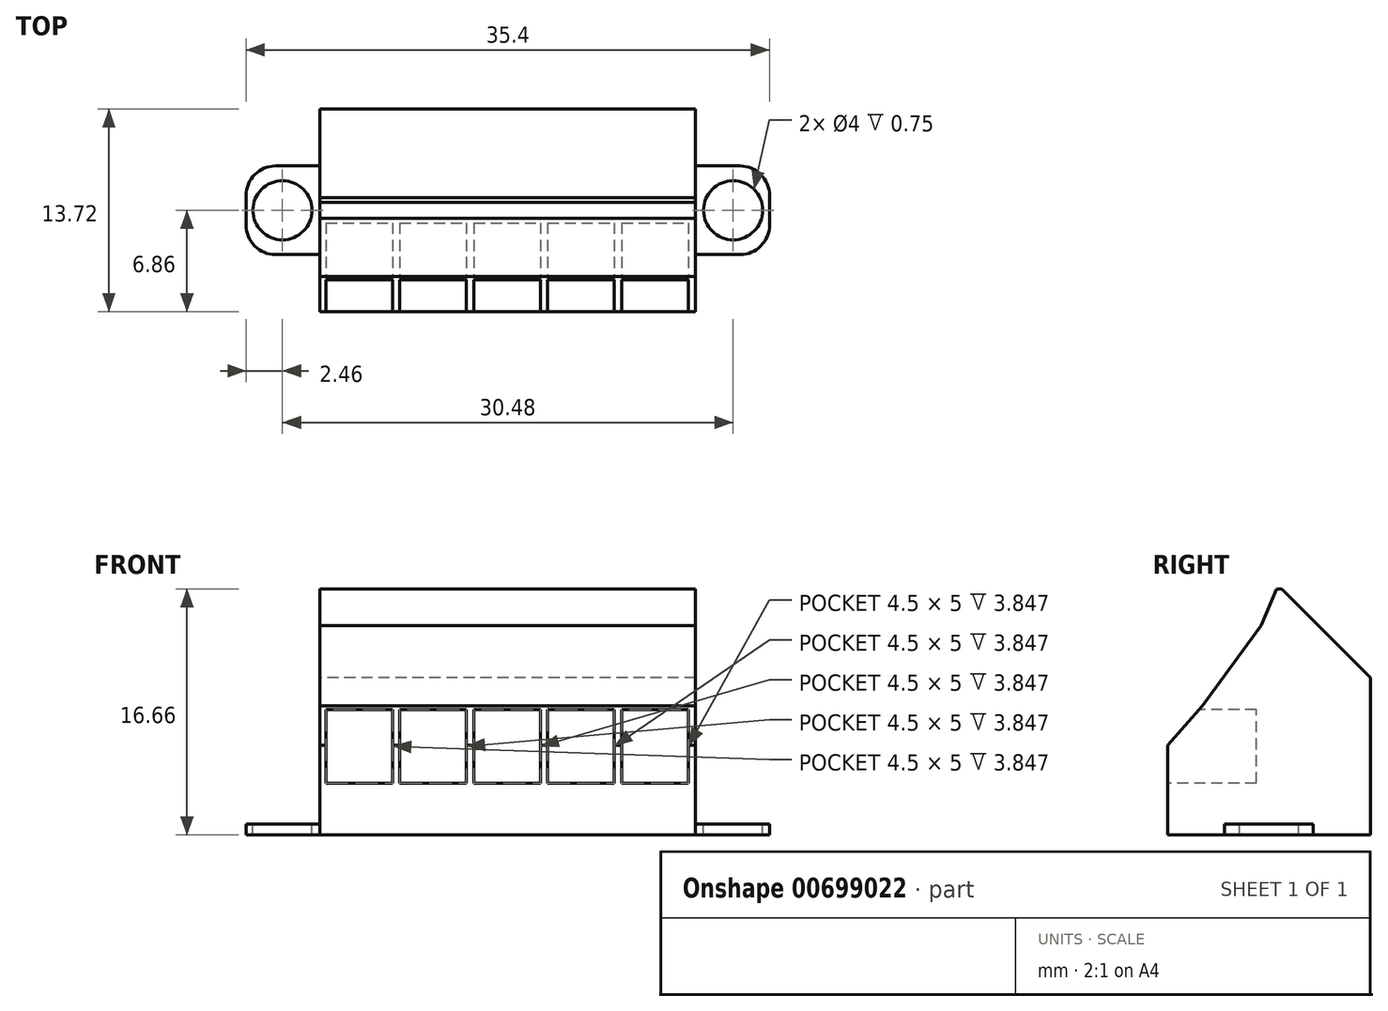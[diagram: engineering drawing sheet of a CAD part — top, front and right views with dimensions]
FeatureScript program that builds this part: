
annotation { "Feature Type Name" : "Feature", "Feature Type Description" : "" }
export const myFeature = defineFeature(function(context is Context, id is Id, definition is map)
    precondition{}
    {
        {
            var Q0;
            Q0=qCreatedBy(makeId("Top.planeOp"),FACE);
            var sketch = newSketch(context, id + "F0", { "sketchPlane" : qUnion([Q0])});
            skLineSegment(sketch, "E0.bottom", {"start": v(12.7, -6.86) * mm, "end": v(-12.7, -6.86) * mm});
            skLineSegment(sketch, "E0.top", {"start": v(12.7, 6.86) * mm, "end": v(-12.7, 6.86) * mm});
            skLineSegment(sketch, "E0.left", {"start": v(12.7, -6.86) * mm, "end": v(12.7, 6.86) * mm});
            skLineSegment(sketch, "E0.right", {"start": v(-12.7, -6.86) * mm, "end": v(-12.7, 6.86) * mm});
            skPoint(sketch, "E0.middle", {"position": v(0, 0) * mm});
            skSolve(sketch);
        }
        {
            var Q0;
            Q0=qSketchRegion(id+"F0",true);
            extrude(context, id + "F1", {"entities" : qUnion([Q0]), "depth" : 16.66 * mm, "offsetDistance" : 25 * mm});
        }
        {
            var Q0;
            Q0=makeQuery(id+"F1.opExtrude","SWEPT_FACE",FACE,{"disambiguationData":[OSD([sQuery(id+"F0.wireOp",EDGE,"E0.right")])]});
            var sketch = newSketch(context, id + "F2", { "sketchPlane" : qUnion([Q0])});
            skLineSegment(sketch, "E1", {"start": v(-0.86, 16.66) * mm, "end": v(-6.86, 10.66) * mm});
            skLineSegment(sketch, "E2", {"start": v(-0.53, 16.66) * mm, "end": v(0.54, 14.16) * mm});
            skLineSegment(sketch, "E3", {"start": v(0.54, 14.16) * mm, "end": v(4.5, 8.74) * mm});
            skLineSegment(sketch, "E4", {"start": v(4.5, 8.74) * mm, "end": v(6.86, 6.08) * mm});
            skSolve(sketch);
        }
        {
            var Q0;
            {var subQ0=sQuery(id+"F2.wireOp",EDGE,"E1");Q0=makeQuery(id+"F2.imprint","IMPRINT",FACE,{"disambiguationData":[TD([[makeQuery(id+"F2.imprint","IMPRINT",EDGE,{"derivedFrom":subQ0}),-1.0]])]});}
            var Q1;
            {var subQ5=sQuery(id+"F2.wireOp",EDGE,"E2");Q1=makeQuery(id+"F2.imprint","IMPRINT",FACE,{"disambiguationData":[TD([[makeQuery(id+"F2.imprint","IMPRINT",EDGE,{"derivedFrom":subQ5}),1.0]])]});}
            extrude(context, id + "F3", {"entities" : qUnion([Q0, Q1]), "operationType" : NewBodyOperationType.REMOVE, "endBound" : BoundingType.THROUGH_ALL, "oppositeDirection" : true, "depth" : 25 * mm, "offsetDistance" : 25 * mm});
        }
        {
            var Q0;
            Q0=makeQuery(id+"F1.opExtrude","SWEPT_FACE",FACE,{"disambiguationData":[OSD([sQuery(id+"F0.wireOp",EDGE,"E0.top")])]});
            var sketch = newSketch(context, id + "F4", { "sketchPlane" : qUnion([Q0])});
            skCircle(sketch, "E5", {"center": v(9.72, 5.33) * mm, "radius": 2.25 * mm});
            skPoint(sketch, "E5.centerSnap0", {"position": v(12.7, 5.33) * mm});
            skCircle(sketch, "E6.1.0.0", {"center": v(4.72, 5.33) * mm, "radius": 2.25 * mm});
            skCircle(sketch, "E6.2.0.0", {"center": v(-0.28, 5.33) * mm, "radius": 2.25 * mm});
            skCircle(sketch, "E6.3.0.0", {"center": v(-5.28, 5.33) * mm, "radius": 2.25 * mm});
            skCircle(sketch, "E6.4.0.0", {"center": v(-10.28, 5.33) * mm, "radius": 2.25 * mm});
            skCircle(sketch, "E6.5.0.0", {"center": v(-15.28, 5.33) * mm, "radius": 2.25 * mm});
            skCircle(sketch, "E6.6.0.0", {"center": v(-20.28, 5.33) * mm, "radius": 2.25 * mm});
            skCircle(sketch, "E6.7.0.0", {"center": v(-25.28, 5.33) * mm, "radius": 2.25 * mm});
            skCircle(sketch, "E6.8.0.0", {"center": v(-30.28, 5.33) * mm, "radius": 2.25 * mm});
            skCircle(sketch, "E6.9.0.0", {"center": v(-35.28, 5.33) * mm, "radius": 2.25 * mm});
            skCircle(sketch, "E6.10.0.0", {"center": v(-40.28, 5.33) * mm, "radius": 2.25 * mm});
            skCircle(sketch, "E6.11.0.0", {"center": v(-45.28, 5.33) * mm, "radius": 2.25 * mm});
            skLineSegment(sketch, "E6.direction1", {"start": v(9.72, 5.33) * mm, "end": v(4.72, 5.33) * mm, "construction": true});
            skSolve(sketch);
        }
        {
            var Q0;
            Q0=makeQuery(id+"F1.opExtrude","SWEPT_FACE",FACE,{"disambiguationData":[OSD([sQuery(id+"F0.wireOp",EDGE,"E0.bottom")])]});
            var sketch = newSketch(context, id + "F5", { "sketchPlane" : qUnion([Q0])});
            skLineSegment(sketch, "E7.bottom", {"start": v(-12.3, 3.5) * mm, "end": v(-7.8, 3.5) * mm});
            skLineSegment(sketch, "E7.top", {"start": v(-12.3, 8.5) * mm, "end": v(-7.8, 8.5) * mm});
            skLineSegment(sketch, "E7.left", {"start": v(-12.3, 3.5) * mm, "end": v(-12.3, 8.5) * mm});
            skLineSegment(sketch, "E7.right", {"start": v(-7.8, 3.5) * mm, "end": v(-7.8, 8.5) * mm});
            skLineSegment(sketch, "E8.1.0.0", {"start": v(-7.3, 3.5) * mm, "end": v(-2.8, 3.5) * mm});
            skLineSegment(sketch, "E8.1.0.1", {"start": v(-7.3, 3.5) * mm, "end": v(-7.3, 8.5) * mm});
            skLineSegment(sketch, "E8.1.0.2", {"start": v(-2.8, 3.5) * mm, "end": v(-2.8, 8.5) * mm});
            skLineSegment(sketch, "E8.1.0.3", {"start": v(-7.3, 8.5) * mm, "end": v(-2.8, 8.5) * mm});
            skLineSegment(sketch, "E8.2.0.0", {"start": v(-2.3, 3.5) * mm, "end": v(2.2, 3.5) * mm});
            skLineSegment(sketch, "E8.2.0.1", {"start": v(-2.3, 3.5) * mm, "end": v(-2.3, 8.5) * mm});
            skLineSegment(sketch, "E8.2.0.2", {"start": v(2.2, 3.5) * mm, "end": v(2.2, 8.5) * mm});
            skLineSegment(sketch, "E8.2.0.3", {"start": v(-2.3, 8.5) * mm, "end": v(2.2, 8.5) * mm});
            skLineSegment(sketch, "E8.3.0.0", {"start": v(2.7, 3.5) * mm, "end": v(7.2, 3.5) * mm});
            skLineSegment(sketch, "E8.3.0.1", {"start": v(2.7, 3.5) * mm, "end": v(2.7, 8.5) * mm});
            skLineSegment(sketch, "E8.3.0.2", {"start": v(7.2, 3.5) * mm, "end": v(7.2, 8.5) * mm});
            skLineSegment(sketch, "E8.3.0.3", {"start": v(2.7, 8.5) * mm, "end": v(7.2, 8.5) * mm});
            skLineSegment(sketch, "E8.4.0.0", {"start": v(7.7, 3.5) * mm, "end": v(12.2, 3.5) * mm});
            skLineSegment(sketch, "E8.4.0.1", {"start": v(7.7, 3.5) * mm, "end": v(7.7, 8.5) * mm});
            skLineSegment(sketch, "E8.4.0.2", {"start": v(12.2, 3.5) * mm, "end": v(12.2, 8.5) * mm});
            skLineSegment(sketch, "E8.4.0.3", {"start": v(7.7, 8.5) * mm, "end": v(12.2, 8.5) * mm});
            skLineSegment(sketch, "E8.5.0.0", {"start": v(12.7, 3.5) * mm, "end": v(17.2, 3.5) * mm});
            skLineSegment(sketch, "E8.5.0.1", {"start": v(12.7, 3.5) * mm, "end": v(12.7, 8.5) * mm});
            skLineSegment(sketch, "E8.5.0.2", {"start": v(17.2, 3.5) * mm, "end": v(17.2, 8.5) * mm});
            skLineSegment(sketch, "E8.5.0.3", {"start": v(12.7, 8.5) * mm, "end": v(17.2, 8.5) * mm});
            skLineSegment(sketch, "E8.6.0.0", {"start": v(17.7, 3.5) * mm, "end": v(22.2, 3.5) * mm});
            skLineSegment(sketch, "E8.6.0.1", {"start": v(17.7, 3.5) * mm, "end": v(17.7, 8.5) * mm});
            skLineSegment(sketch, "E8.6.0.2", {"start": v(22.2, 3.5) * mm, "end": v(22.2, 8.5) * mm});
            skLineSegment(sketch, "E8.6.0.3", {"start": v(17.7, 8.5) * mm, "end": v(22.2, 8.5) * mm});
            skLineSegment(sketch, "E8.7.0.0", {"start": v(22.7, 3.5) * mm, "end": v(27.2, 3.5) * mm});
            skLineSegment(sketch, "E8.7.0.1", {"start": v(22.7, 3.5) * mm, "end": v(22.7, 8.5) * mm});
            skLineSegment(sketch, "E8.7.0.2", {"start": v(27.2, 3.5) * mm, "end": v(27.2, 8.5) * mm});
            skLineSegment(sketch, "E8.7.0.3", {"start": v(22.7, 8.5) * mm, "end": v(27.2, 8.5) * mm});
            skLineSegment(sketch, "E8.8.0.0", {"start": v(27.7, 3.5) * mm, "end": v(32.2, 3.5) * mm});
            skLineSegment(sketch, "E8.8.0.1", {"start": v(27.7, 3.5) * mm, "end": v(27.7, 8.5) * mm});
            skLineSegment(sketch, "E8.8.0.2", {"start": v(32.2, 3.5) * mm, "end": v(32.2, 8.5) * mm});
            skLineSegment(sketch, "E8.8.0.3", {"start": v(27.7, 8.5) * mm, "end": v(32.2, 8.5) * mm});
            skLineSegment(sketch, "E8.9.0.0", {"start": v(32.7, 3.5) * mm, "end": v(37.2, 3.5) * mm});
            skLineSegment(sketch, "E8.9.0.1", {"start": v(32.7, 3.5) * mm, "end": v(32.7, 8.5) * mm});
            skLineSegment(sketch, "E8.9.0.2", {"start": v(37.2, 3.5) * mm, "end": v(37.2, 8.5) * mm});
            skLineSegment(sketch, "E8.9.0.3", {"start": v(32.7, 8.5) * mm, "end": v(37.2, 8.5) * mm});
            skLineSegment(sketch, "E8.10.0.0", {"start": v(37.7, 3.5) * mm, "end": v(42.2, 3.5) * mm});
            skLineSegment(sketch, "E8.10.0.1", {"start": v(37.7, 3.5) * mm, "end": v(37.7, 8.5) * mm});
            skLineSegment(sketch, "E8.10.0.2", {"start": v(42.2, 3.5) * mm, "end": v(42.2, 8.5) * mm});
            skLineSegment(sketch, "E8.10.0.3", {"start": v(37.7, 8.5) * mm, "end": v(42.2, 8.5) * mm});
            skLineSegment(sketch, "E8.11.0.0", {"start": v(42.7, 3.5) * mm, "end": v(47.2, 3.5) * mm});
            skLineSegment(sketch, "E8.11.0.1", {"start": v(42.7, 3.5) * mm, "end": v(42.7, 8.5) * mm});
            skLineSegment(sketch, "E8.11.0.2", {"start": v(47.2, 3.5) * mm, "end": v(47.2, 8.5) * mm});
            skLineSegment(sketch, "E8.11.0.3", {"start": v(42.7, 8.5) * mm, "end": v(47.2, 8.5) * mm});
            skLineSegment(sketch, "E8.direction1", {"start": v(-12.3, 3.5) * mm, "end": v(-7.3, 3.5) * mm, "construction": true});
            skSolve(sketch);
        }
        {
            var Q0;
            Q0=qSketchRegion(id+"F5",true);
            var Q1;
            Q1=qSketchRegion(id+"F4",true);
            extrude(context, id + "F6", {"entities" : qUnion([Q0, Q1]), "operationType" : NewBodyOperationType.REMOVE, "oppositeDirection" : true, "depth" : 6 * mm, "offsetDistance" : 25 * mm});
        }
        {
            var Q0;
            Q0=makeQuery(id+"F3.boolean.opBoolean","COPY",FACE,{"derivedFrom":makeQuery(id+"F3.opExtrude","SWEPT_FACE",FACE,{"disambiguationData":[OSD([sQuery(id+"F2.wireOp",EDGE,"E1")])]})});
            var sketch = newSketch(context, id + "F7", { "sketchPlane" : qUnion([Q0])});
            skCircle(sketch, "E9", {"center": v(-10.05, -6.93) * mm, "radius": 2.25 * mm});
            skCircle(sketch, "E10.1.0.0", {"center": v(-5.05, -6.93) * mm, "radius": 2.25 * mm});
            skCircle(sketch, "E10.2.0.0", {"center": v(-0.05, -6.93) * mm, "radius": 2.25 * mm});
            skCircle(sketch, "E10.3.0.0", {"center": v(4.95, -6.93) * mm, "radius": 2.25 * mm});
            skCircle(sketch, "E10.4.0.0", {"center": v(9.95, -6.93) * mm, "radius": 2.25 * mm});
            skCircle(sketch, "E10.5.0.0", {"center": v(14.95, -6.93) * mm, "radius": 2.25 * mm});
            skCircle(sketch, "E10.6.0.0", {"center": v(19.95, -6.93) * mm, "radius": 2.25 * mm});
            skCircle(sketch, "E10.7.0.0", {"center": v(24.95, -6.93) * mm, "radius": 2.25 * mm});
            skCircle(sketch, "E10.8.0.0", {"center": v(29.95, -6.93) * mm, "radius": 2.25 * mm});
            skCircle(sketch, "E10.9.0.0", {"center": v(34.95, -6.93) * mm, "radius": 2.25 * mm});
            skCircle(sketch, "E10.10.0.0", {"center": v(39.95, -6.93) * mm, "radius": 2.25 * mm});
            skCircle(sketch, "E10.11.0.0", {"center": v(44.95, -6.93) * mm, "radius": 2.25 * mm});
            skLineSegment(sketch, "E10.direction1", {"start": v(-10.05, -6.93) * mm, "end": v(-5.05, -6.93) * mm, "construction": true});
            skSolve(sketch);
        }
        {
            var Q0;
            Q0=qSketchRegion(id+"F7",true);
            extrude(context, id + "F8", {"entities" : qUnion([Q0]), "operationType" : NewBodyOperationType.REMOVE, "oppositeDirection" : true, "depth" : 2 * mm, "offsetDistance" : 25 * mm});
        }
        {
            var Q0;
            Q0=makeQuery(id+"F1.opExtrude","SWEPT_FACE",FACE,{"disambiguationData":[OSD([sQuery(id+"F0.wireOp",EDGE,"E0.right")])]});
            var sketch = newSketch(context, id + "F9", { "sketchPlane" : qUnion([Q0])});
            skLineSegment(sketch, "E11.bottom", {"start": v(3, 0.75) * mm, "end": v(-3, 0.75) * mm});
            skLineSegment(sketch, "E11.top", {"start": v(3, -0.75) * mm, "end": v(-3, -0.75) * mm});
            skLineSegment(sketch, "E11.left", {"start": v(3, 0.75) * mm, "end": v(3, -0.75) * mm});
            skLineSegment(sketch, "E11.right", {"start": v(-3, 0.75) * mm, "end": v(-3, -0.75) * mm});
            skPoint(sketch, "E11.middle", {"position": v(0, 0) * mm});
            skSolve(sketch);
        }
        {
            var Q0;
            {var subQ0=sQuery(id+"F9.wireOp",EDGE,"E11.bottom");Q0=makeQuery(id+"F9.imprint","IMPRINT",FACE,{"disambiguationData":[TD([[makeQuery(id+"F9.imprint","IMPRINT",EDGE,{"derivedFrom":subQ0}),1.0]])]});}
            extrude(context, id + "F10", {"entities" : qUnion([Q0]), "operationType" : NewBodyOperationType.ADD, "depth" : 5 * mm, "offsetDistance" : 25 * mm});
        }
        {
            var Q0;
            Q0=makeQuery(id+"F1.opExtrude","SWEPT_FACE",FACE,{"disambiguationData":[OSD([sQuery(id+"F0.wireOp",EDGE,"E0.left")])]});
            var sketch = newSketch(context, id + "F11", { "sketchPlane" : qUnion([Q0])});
            skLineSegment(sketch, "E12.bottom", {"start": v(-3, -0.75) * mm, "end": v(3, -0.75) * mm});
            skLineSegment(sketch, "E12.top", {"start": v(-3, 0.75) * mm, "end": v(3, 0.75) * mm});
            skLineSegment(sketch, "E12.left", {"start": v(-3, -0.75) * mm, "end": v(-3, 0.75) * mm});
            skLineSegment(sketch, "E12.right", {"start": v(3, -0.75) * mm, "end": v(3, 0.75) * mm});
            skPoint(sketch, "E12.middle", {"position": v(0, 0) * mm});
            skSolve(sketch);
        }
        {
            var Q0;
            {var subQ0=sQuery(id+"F11.wireOp",EDGE,"E12.top");Q0=makeQuery(id+"F11.imprint","IMPRINT",FACE,{"disambiguationData":[TD([[makeQuery(id+"F11.imprint","IMPRINT",EDGE,{"derivedFrom":subQ0}),-1.0]])]});}
            extrude(context, id + "F12", {"entities" : qUnion([Q0]), "operationType" : NewBodyOperationType.ADD, "depth" : 5 * mm, "offsetDistance" : 25 * mm});
        }
        {
            var Q0;
            Q0=makeQuery(id+"F10.opExtrude","CAP_EDGE",EDGE,{"disambiguationData":[OSD([sQuery(id+"F9.wireOp",EDGE,"E11.right")])],"isStart":false});
            var Q1;
            Q1=makeQuery(id+"F10.opExtrude","CAP_EDGE",EDGE,{"disambiguationData":[OSD([sQuery(id+"F9.wireOp",EDGE,"E11.left")])],"isStart":false});
            var Q2;
            Q2=makeQuery(id+"F12.opExtrude","CAP_EDGE",EDGE,{"disambiguationData":[OSD([sQuery(id+"F11.wireOp",EDGE,"E12.left")])],"isStart":false});
            var Q3;
            Q3=makeQuery(id+"F12.opExtrude","CAP_EDGE",EDGE,{"disambiguationData":[OSD([sQuery(id+"F11.wireOp",EDGE,"E12.right")])],"isStart":false});
            fillet(context, id + "F13", {"entities" : qUnion([Q0, Q1, Q2, Q3]), "radius" : 2 * mm, "tangentPropagation" : true, "allowEdgeOverflow" : false});
        }
        {
            var Q0;
            Q0=makeQuery(id+"F10.opExtrude","SWEPT_FACE",FACE,{"disambiguationData":[OSD([sQuery(id+"F9.wireOp",EDGE,"E11.bottom")])]});
            var sketch = newSketch(context, id + "F14", { "sketchPlane" : qUnion([Q0])});
            skCircle(sketch, "E13", {"center": v(-15.24, 0) * mm, "radius": 2 * mm});
            skPoint(sketch, "E13.centerSnap0", {"position": v(-17.7, 0) * mm});
            skSolve(sketch);
        }
        {
            var Q0;
            Q0=qSketchRegion(id+"F14",true);
            extrude(context, id + "F15", {"entities" : qUnion([Q0]), "operationType" : NewBodyOperationType.REMOVE, "endBound" : BoundingType.THROUGH_ALL, "oppositeDirection" : true, "depth" : 0.5 * mm, "offsetDistance" : 25 * mm});
        }
        {
            var Q0;
            Q0=makeQuery(id+"F12.opExtrude","SWEPT_FACE",FACE,{"disambiguationData":[OSD([sQuery(id+"F11.wireOp",EDGE,"E12.top")])]});
            var sketch = newSketch(context, id + "F16", { "sketchPlane" : qUnion([Q0])});
            skCircle(sketch, "E14", {"center": v(15.24, 0) * mm, "radius": 2 * mm});
            skPoint(sketch, "E14.centerSnap0", {"position": v(17.7, 0) * mm});
            skSolve(sketch);
        }
        {
            var Q0;
            Q0=qSketchRegion(id+"F16",true);
            extrude(context, id + "F17", {"entities" : qUnion([Q0]), "operationType" : NewBodyOperationType.REMOVE, "endBound" : BoundingType.THROUGH_ALL, "oppositeDirection" : true, "depth" : 0.5 * mm, "offsetDistance" : 25 * mm});
        }
    });
